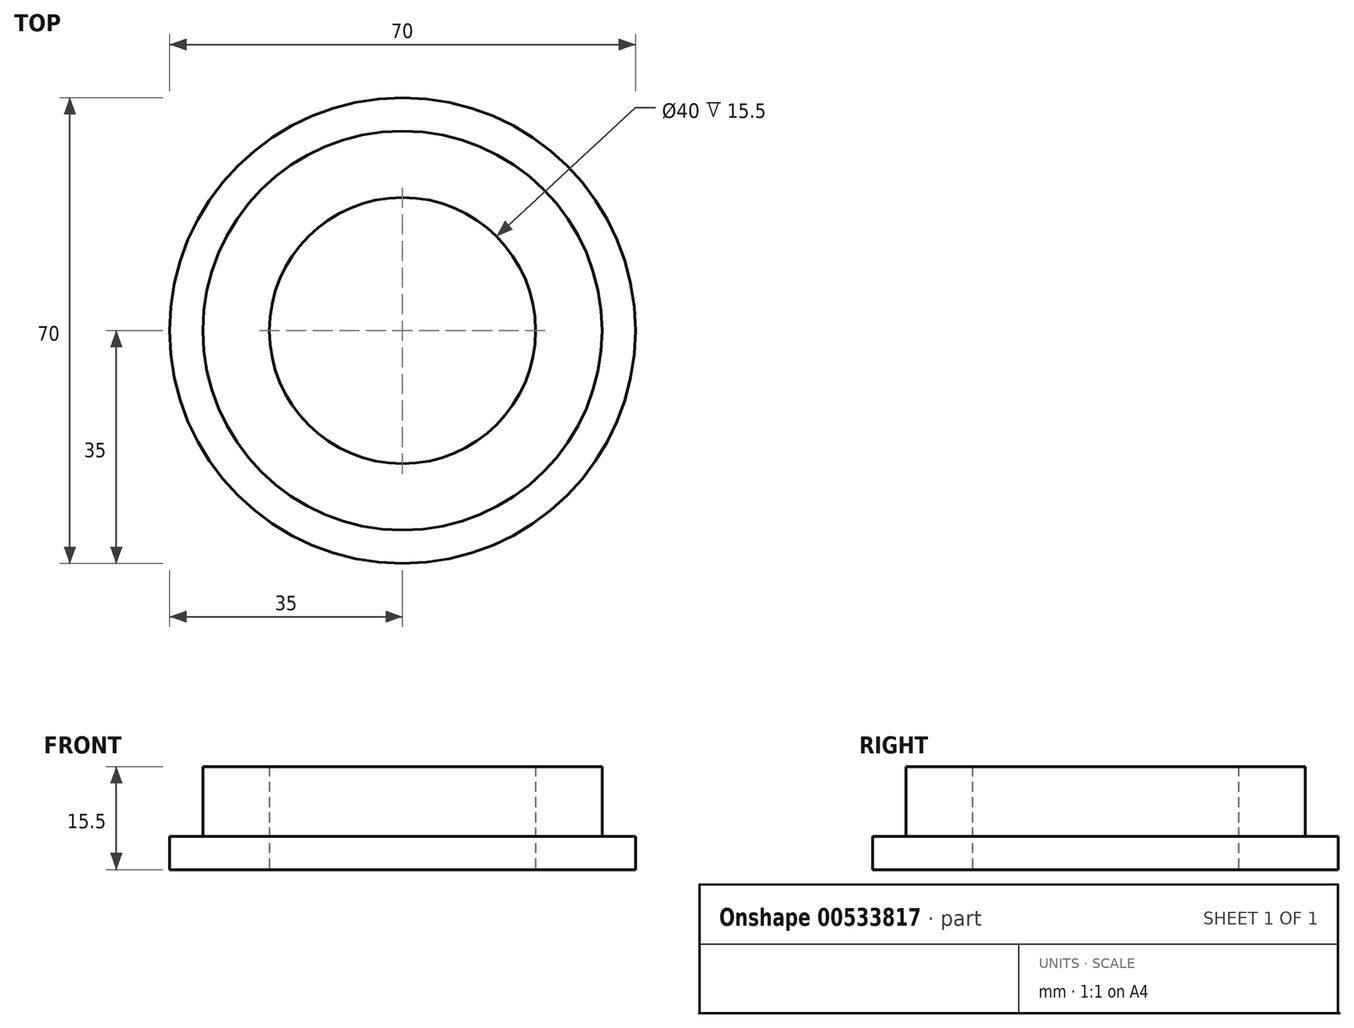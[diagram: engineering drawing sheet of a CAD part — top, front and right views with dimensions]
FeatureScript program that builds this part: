
annotation { "Feature Type Name" : "Feature", "Feature Type Description" : "" }
export const myFeature = defineFeature(function(context is Context, id is Id, definition is map)
    precondition{}
    {
        {
            var Q0;
            Q0=qCreatedBy(makeId("Top.planeOp"),FACE);
            var sketch = newSketch(context, id + "F0", { "sketchPlane" : qUnion([Q0])});
            skCircle(sketch, "E0", {"center": v(0, 0) * mm, "radius": 30 * mm});
            skSolve(sketch);
        }
        {
            var Q0;
            Q0=makeQuery(id+"F0.imprint","IMPRINT",FACE,{"disambiguationData":[TD([[makeQuery(id+"F0.imprint","IMPRINT",EDGE,{"derivedFrom":sQuery(id+"F0.wireOp",EDGE,"E0")}),1.0]])]});
            extrude(context, id + "F1", {"entities" : qUnion([Q0]), "depth" : 15.5 * mm, "offsetDistance" : 25.4 * mm});
        }
        {
            var Q0;
            Q0=qCreatedBy(makeId("Top.planeOp"),FACE);
            var sketch = newSketch(context, id + "F2", { "sketchPlane" : qUnion([Q0])});
            skCircle(sketch, "E1", {"center": v(0, 0) * mm, "radius": 35 * mm});
            skSolve(sketch);
        }
        {
            var Q0;
            Q0=qCreatedBy(makeId("Top.planeOp"),FACE);
            var sketch = newSketch(context, id + "F3", { "sketchPlane" : qUnion([Q0])});
            skCircle(sketch, "E2", {"center": v(0, 0) * mm, "radius": 20 * mm});
            skSolve(sketch);
        }
        {
            var Q0;
            Q0=makeQuery(id+"F2.imprint","IMPRINT",FACE,{"disambiguationData":[TD([[makeQuery(id+"F2.imprint","IMPRINT",EDGE,{"derivedFrom":sQuery(id+"F2.wireOp",EDGE,"E1")}),1.0]])]});
            extrude(context, id + "F4", {"entities" : qUnion([Q0]), "operationType" : NewBodyOperationType.ADD, "depth" : 5 * mm, "offsetDistance" : 25.4 * mm});
        }
        {
            var Q0;
            Q0 = qSketchRegion(id + "F3", true);
            extrude(context, id + "F5", {"entities" : qUnion([Q0]), "operationType" : NewBodyOperationType.ADD, "depth" : 25.4 * mm, "offsetDistance" : 25.4 * mm});
        }
        {
            var Q0;
            Q0=sQuery(id+"F3.wireOp",VERTEX,"E2.center");
            var Q1;
            Q1=makeQuery(id+"F1.opExtrude","SWEPT_BODY",BODY,{"disambiguationData":[OSD([sQuery(id+"F0.wireOp",EDGE,"E0")])]});
            hole(context, id + "F6", {"style" : HoleStyle.SIMPLE, "endStyle" : HoleEndStyle.THROUGH, "oppositeDirection" : true, "holeDiameter" : 40 * mm, "isTappedThrough" : true, "tappedDepth" : 12.7 * mm, "tapClearance" : 3, "locations" : qUnion([Q0]), "scope" : qUnion([Q1])});
        }
    });
